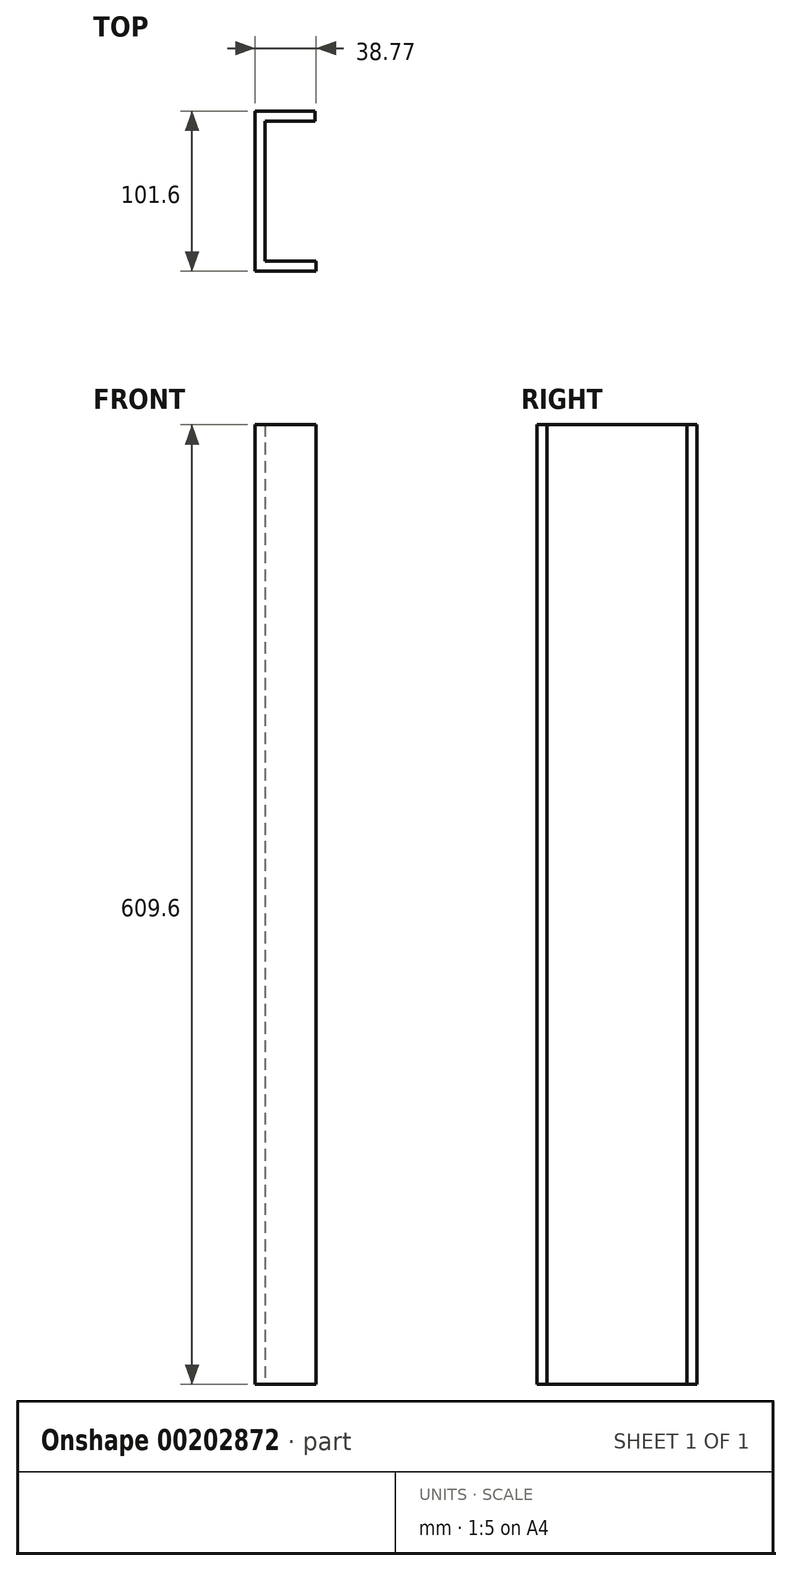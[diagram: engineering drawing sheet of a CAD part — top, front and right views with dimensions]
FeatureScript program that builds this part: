
annotation { "Feature Type Name" : "Feature", "Feature Type Description" : "" }
export const myFeature = defineFeature(function(context is Context, id is Id, definition is map)
    precondition{}
    {
        {
            var Q0;
            Q0=qCreatedBy(makeId("Top.planeOp"),FACE);
            var sketch = newSketch(context, id + "F0", { "sketchPlane" : qUnion([Q0])});
            skLineSegment(sketch, "E0", {"start": v(38.1, 59.34) * mm, "end": v(0, 59.34) * mm});
            skLineSegment(sketch, "E1", {"start": v(0, 59.34) * mm, "end": v(0, -42.26) * mm});
            skLineSegment(sketch, "E2", {"start": v(0, -42.26) * mm, "end": v(38.77, -42.26) * mm});
            skLineSegment(sketch, "E3.0", {"start": v(6.35, -35.9) * mm, "end": v(38.77, -35.9) * mm});
            skLineSegment(sketch, "E3.1", {"start": v(6.35, 53) * mm, "end": v(6.35, -35.9) * mm});
            skLineSegment(sketch, "E3.2", {"start": v(38.1, 53) * mm, "end": v(6.35, 53) * mm});
            skLineSegment(sketch, "E4", {"start": v(38.1, 59.34) * mm, "end": v(38.1, 53) * mm});
            skLineSegment(sketch, "E5", {"start": v(38.77, -35.9) * mm, "end": v(38.77, -42.26) * mm});
            skSolve(sketch);
        }
        {
            var Q0;
            Q0=makeQuery(id+"F0.imprint","IMPRINT",FACE,{"disambiguationData":[TD([[makeQuery(id+"F0.imprint","IMPRINT",EDGE,{"derivedFrom":sQuery(id+"F0.wireOp",EDGE,"E0")}),1.0]])]});
            extrude(context, id + "F1", {"entities" : qUnion([Q0]), "depth" : 609.6 * mm});
        }
    });
